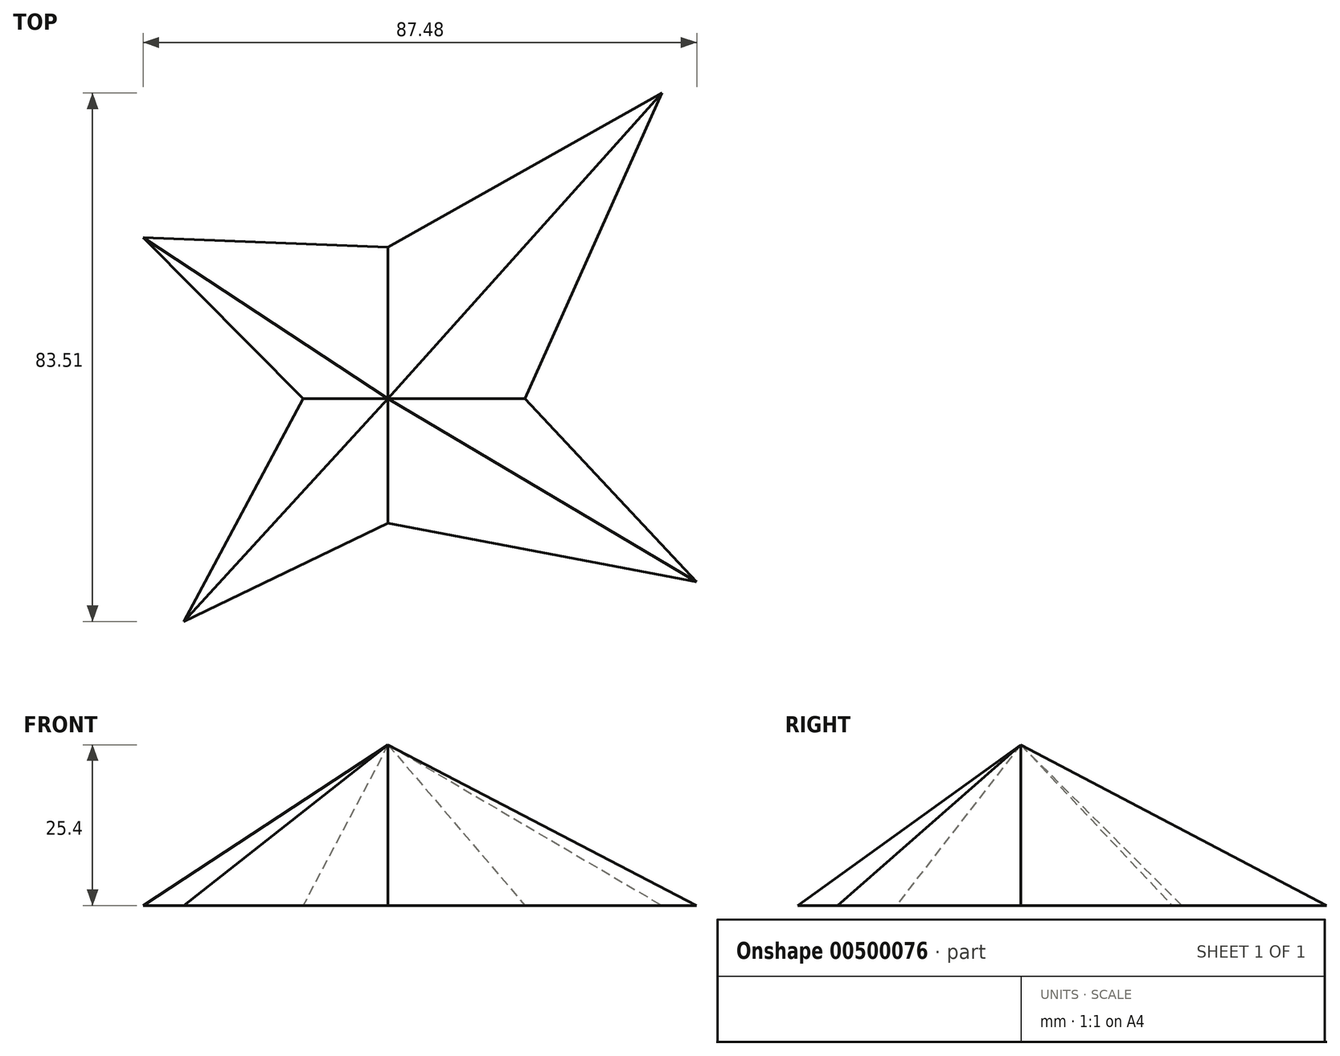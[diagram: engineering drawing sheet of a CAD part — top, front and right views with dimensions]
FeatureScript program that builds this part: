
annotation { "Feature Type Name" : "Feature", "Feature Type Description" : "" }
export const myFeature = defineFeature(function(context is Context, id is Id, definition is map)
    precondition{}
    {
        {
            var Q0;
            Q0=qCreatedBy(makeId("Top.planeOp"),FACE);
            var sketch = newSketch(context, id + "F0", { "sketchPlane" : qUnion([Q0])});
            skLineSegment(sketch, "E0", {"start": v(0, 23.93) * mm, "end": v(43.28, 48.31) * mm});
            skLineSegment(sketch, "E1", {"start": v(43.28, 48.31) * mm, "end": v(21.64, 0) * mm});
            skLineSegment(sketch, "E2", {"start": v(21.64, 0) * mm, "end": v(48.77, -28.96) * mm});
            skLineSegment(sketch, "E3", {"start": v(48.77, -28.96) * mm, "end": v(0, -19.66) * mm});
            skLineSegment(sketch, "E4", {"start": v(0, -19.66) * mm, "end": v(-32.3, -35.2) * mm});
            skLineSegment(sketch, "E5", {"start": v(-32.3, -35.2) * mm, "end": v(-13.41, 0) * mm});
            skLineSegment(sketch, "E6", {"start": v(-13.41, 0) * mm, "end": v(-38.7, 25.45) * mm});
            skLineSegment(sketch, "E7", {"start": v(-38.7, 25.45) * mm, "end": v(0, 23.93) * mm});
            skSolve(sketch);
        }
        {
            var Q0;
            Q0=qCreatedBy(makeId("Top.planeOp"),FACE);
            cPlane(context, id + "F1", {"entities" : qUnion([Q0]), "cplaneType" : CPlaneType.OFFSET, "offset" : 25.4 * mm, "width" : 152.4 * mm, "height" : 152.4 * mm});
        }
        {
            var Q0;
            Q0=qCreatedBy(id+"F1.planeOp",FACE);
            var sketch = newSketch(context, id + "F2", { "sketchPlane" : qUnion([Q0])});
            skPoint(sketch, "E8", {"position": v(0, 0) * mm});
            skSolve(sketch);
        }
        {
            var Q0;
            Q0=sQuery(id+"F2.wireOp",VERTEX,"E8");
            var Q1;
            Q1=makeQuery(id+"F0.imprint","IMPRINT",FACE,{"disambiguationData":[TD([[makeQuery(id+"F0.imprint","IMPRINT",EDGE,{"derivedFrom":sQuery(id+"F0.wireOp",EDGE,"E0")}),-1.0]])]});
            loft(context, id + "F3", {"sheetProfilesArray" : [{ "sheetProfileEntities" : qUnion([Q0]) }, { "sheetProfileEntities" : qUnion([Q1]) }]});
        }
    });
